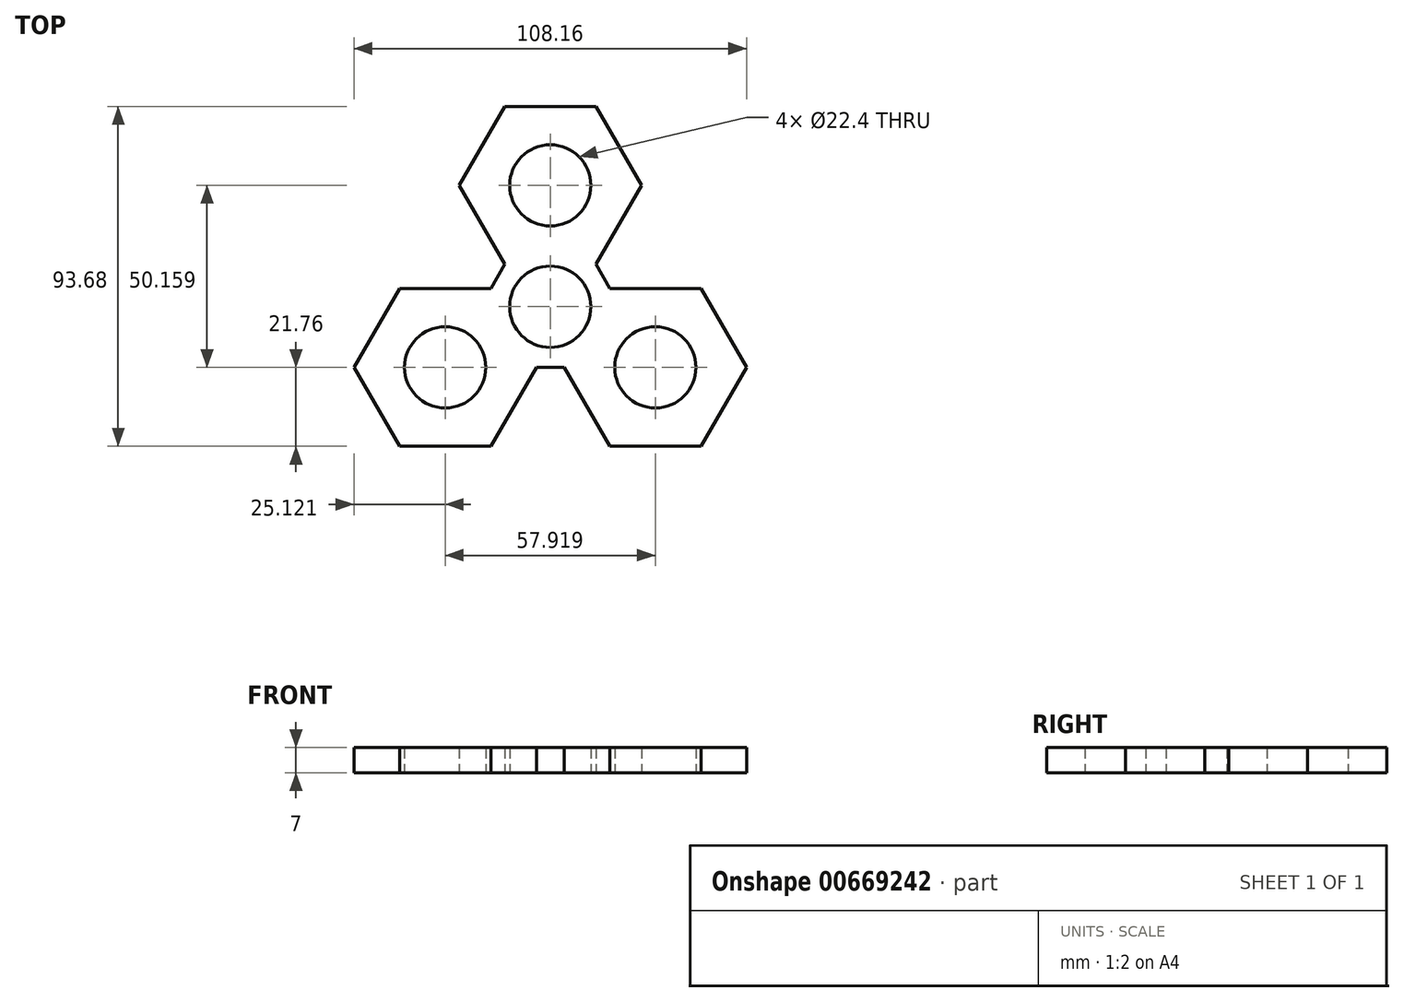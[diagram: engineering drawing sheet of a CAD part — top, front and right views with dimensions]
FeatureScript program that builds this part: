
annotation { "Feature Type Name" : "Feature", "Feature Type Description" : "" }
export const myFeature = defineFeature(function(context is Context, id is Id, definition is map)
    precondition{}
    {
        {
            var Q0;
            Q0=qCreatedBy(makeId("Top.planeOp"),FACE);
            var sketch = newSketch(context, id + "F0", { "sketchPlane" : qUnion([Q0])});
            skCircle(sketch, "E0", {"center": v(0, 0) * mm, "radius": 11.2 * mm});
            skCircle(sketch, "E1", {"center": v(0, 33.44) * mm, "radius": 11.2 * mm});
            skLineSegment(sketch, "E2.0", {"start": v(-12.56, 55.2) * mm, "end": v(12.56, 55.2) * mm});
            skLineSegment(sketch, "E2.1", {"start": v(12.56, 55.2) * mm, "end": v(25.12, 33.44) * mm});
            skLineSegment(sketch, "E2.2", {"start": v(25.12, 33.44) * mm, "end": v(12.56, 11.68) * mm});
            skLineSegment(sketch, "E2.4", {"start": v(-12.56, 11.68) * mm, "end": v(-25.12, 33.44) * mm});
            skLineSegment(sketch, "E2.5", {"start": v(-25.12, 33.44) * mm, "end": v(-12.56, 55.2) * mm});
            skPoint(sketch, "E2.0.midPoint", {"position": v(0, 55.2) * mm});
            skCircle(sketch, "E3.1.0", {"center": v(-28.96, -16.72) * mm, "radius": 11.2 * mm});
            skLineSegment(sketch, "E3.1.1", {"start": v(-54.08, -16.72) * mm, "end": v(-41.52, 5.04) * mm});
            skLineSegment(sketch, "E3.1.2", {"start": v(-41.52, -38.48) * mm, "end": v(-54.08, -16.72) * mm});
            skLineSegment(sketch, "E3.1.3", {"start": v(-16.4, -38.48) * mm, "end": v(-41.52, -38.48) * mm});
            skLineSegment(sketch, "E3.1.5", {"start": v(-3.83, -16.72) * mm, "end": v(-16.4, -38.48) * mm});
            skLineSegment(sketch, "E3.1.7", {"start": v(-41.52, 5.04) * mm, "end": v(-16.4, 5.04) * mm});
            skCircle(sketch, "E3.2.0", {"center": v(28.96, -16.72) * mm, "radius": 11.2 * mm});
            skLineSegment(sketch, "E3.2.1", {"start": v(41.52, -38.48) * mm, "end": v(16.4, -38.48) * mm});
            skLineSegment(sketch, "E3.2.2", {"start": v(54.08, -16.72) * mm, "end": v(41.52, -38.48) * mm});
            skLineSegment(sketch, "E3.2.3", {"start": v(41.52, 5.04) * mm, "end": v(54.08, -16.72) * mm});
            skLineSegment(sketch, "E3.2.5", {"start": v(16.4, 5.04) * mm, "end": v(41.52, 5.04) * mm});
            skLineSegment(sketch, "E3.2.7", {"start": v(16.4, -38.48) * mm, "end": v(3.83, -16.72) * mm});
            skLineSegment(sketch, "E4", {"start": v(-12.56, 11.68) * mm, "end": v(-16.4, 5.04) * mm});
            skLineSegment(sketch, "E5", {"start": v(12.56, 11.68) * mm, "end": v(16.4, 5.04) * mm});
            skLineSegment(sketch, "E6", {"start": v(-3.83, -16.72) * mm, "end": v(3.83, -16.72) * mm});
            skSolve(sketch);
        }
        {
            var Q0;
            Q0=makeQuery(id+"F0.imprint","IMPRINT",FACE,{"disambiguationData":[TD([[makeQuery(id+"F0.imprint","IMPRINT",EDGE,{"derivedFrom":sQuery(id+"F0.wireOp",EDGE,"E0")}),-1.0]])]});
            extrude(context, id + "F1", {"entities" : qUnion([Q0]), "depth" : 7 * mm, "offsetDistance" : 25 * mm});
        }
    });
